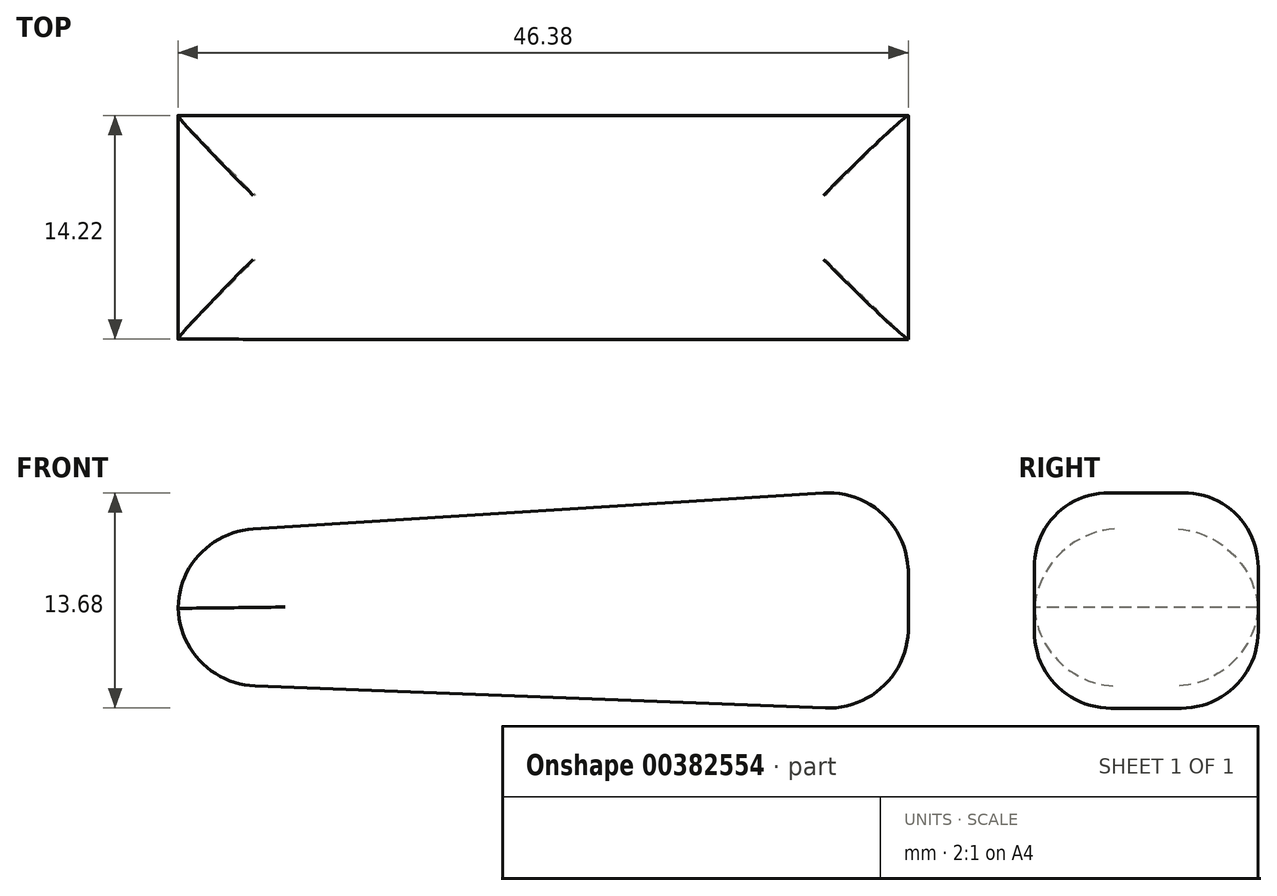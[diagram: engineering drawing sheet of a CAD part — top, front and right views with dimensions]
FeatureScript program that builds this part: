
annotation { "Feature Type Name" : "Feature", "Feature Type Description" : "" }
export const myFeature = defineFeature(function(context is Context, id is Id, definition is map)
    precondition{}
    {
        {
            var Q0;
            Q0=qCreatedBy(makeId("Front.planeOp"),FACE);
            var sketch = newSketch(context, id + "F0", { "sketchPlane" : qUnion([Q0])});
            skLineSegment(sketch, "E0", {"start": v(-46.38, 4.74) * mm, "end": v(-46.38, -4.74) * mm});
            skLineSegment(sketch, "E1", {"start": v(-46.38, 4.74) * mm, "end": v(0, 7.67) * mm});
            skLineSegment(sketch, "E2", {"start": v(0, 7.67) * mm, "end": v(0, -6.55) * mm});
            skLineSegment(sketch, "E3", {"start": v(0, -6.55) * mm, "end": v(-46.38, -4.74) * mm});
            skLineSegment(sketch, "E4", {"start": v(0, 7.67) * mm, "end": v(-14.78, 7.67) * mm});
            skLineSegment(sketch, "E5", {"start": v(-14.78, 7.67) * mm, "end": v(-14.78, -6.55) * mm});
            skLineSegment(sketch, "E6", {"start": v(0, -6.55) * mm, "end": v(-14.78, -6.55) * mm});
            skSolve(sketch);
        }
        {
            var Q0;
            {var subQ0=sQuery(id+"F0.wireOp",EDGE,"E2");Q0=makeQuery(id+"F0.imprint","IMPRINT",FACE,{"disambiguationData":[TD([[makeQuery(id+"F0.imprint","IMPRINT",EDGE,{"derivedFrom":subQ0}),-1.0]])]});}
            var Q1;
            {var subQ0=sQuery(id+"F0.wireOp",EDGE,"E0");Q1=makeQuery(id+"F0.imprint","IMPRINT",FACE,{"disambiguationData":[TD([[makeQuery(id+"F0.imprint","IMPRINT",EDGE,{"derivedFrom":subQ0}),1.0]])]});}
            extrude(context, id + "F1", {"entities" : qUnion([Q0, Q1]), "depth" : 7.11 * mm, "hasSecondDirection" : true, "secondDirectionOppositeDirection" : true, "secondDirectionDepth" : 7.11 * mm});
        }
        {
            var Q0;
            Q0=makeQuery(id+"F1.opExtrude","SWEPT_FACE",FACE,{"disambiguationData":[OSD([sQuery(id+"F0.wireOp",EDGE,"E3")])]});
            var Q1;
            Q1=makeQuery(id+"F1.opExtrude","SWEPT_FACE",FACE,{"disambiguationData":[OSD([sQuery(id+"F0.wireOp",EDGE,"E1")])]});
            fillet(context, id + "F2", {"entities" : qUnion([Q0, Q1]), "radius" : 5.08 * mm, "tangentPropagation" : true, "allowEdgeOverflow" : false});
        }
    });
